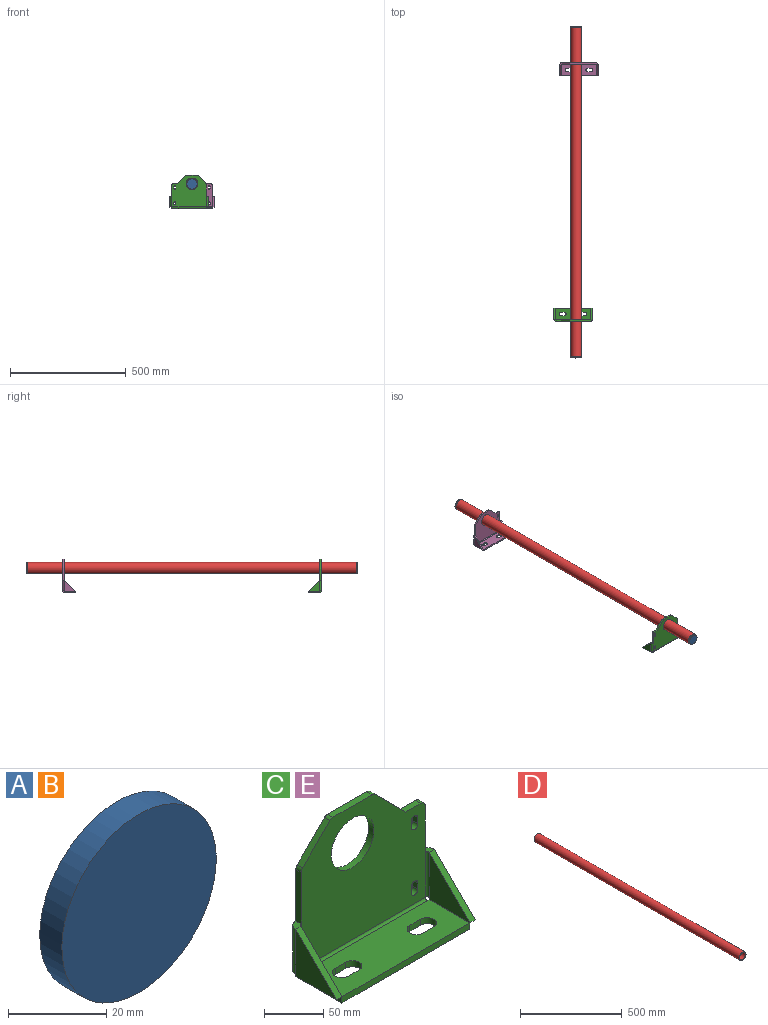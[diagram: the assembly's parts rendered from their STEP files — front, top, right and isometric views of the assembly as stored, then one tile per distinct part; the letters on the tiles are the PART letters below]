
ASSEMBLY  parts=5 mates=8
PART A: 3 faces, bbox 44.5x6.4x44.5 mm
  f0: cylinder r=22.23mm len=44.45mm, axis (0,1,0), area 886.7mm2, adj f1,f2
  f1: plane 44.45x44.45mm, normal (0,-1,0), area 1551.8mm2, adj f0
  f2: plane 44.45x44.45mm, normal (0,1,0), area 1551.8mm2, adj f0
PART B: same geometry as A
PART C: 58 faces, bbox 165.1x57.2x146.1 mm
  f0: plane 6.35x2.26mm, normal (0,1,0), area 14.4mm2, adj f1,f3,f4,f51
  f1: plane 48.51x6.35mm, normal (0,0,-1), area 308.1mm2, adj f0,f2,f3,f4
  f2: plane 48.51x48.51mm, normal (0,-0.71,0.71), area 435.7mm2, adj f1,f3,f4,f50
  f3: plane 48.51x48.51mm, normal (1,0,0), area 1176.8mm2, adj f0,f1,f2,f52
  f4: plane 48.51x48.51mm, normal (-1,0,0), area 1176.8mm2, adj f0,f1,f2,f53
  f5: plane 47.98x6.35mm, normal (1,0,0), area 304.7mm2, adj f20,f21,f50,f57
  f6: plane 6.35x6.35mm, normal (-1,0,0), area 40.3mm2, adj f7,f19,f20,f21
  f7: cylinder r=3.97mm len=7.94mm, axis (0,-1,0), area 79.2mm2, adj f6,f8,f20,f21
  f8: plane 6.35x6.35mm, normal (1,0,0), area 40.3mm2, adj f7,f19,f20,f21
  f9: plane 32.84x32.84mm, normal (-0.71,0,0.71), area 294.9mm2, adj f20,f21,f54,f55
  f10: plane 46.59x6.35mm, normal (0,0,1), area 295.9mm2, adj f20,f21,f55,f56
  f11: plane 36.61x36.61mm, normal (0.71,0,0.71), area 328.8mm2, adj f12,f20,f21,f56
  f12: plane 18.03x6.35mm, normal (0,0,1), area 114.5mm2, adj f11,f20,f21,f57
  f13: plane 6.35x6.35mm, normal (-1,0,0), area 40.3mm2, adj f14,f16,f20,f21
  f14: cylinder r=3.97mm len=7.94mm, axis (0,-1,0), area 79.2mm2, adj f13,f15,f20,f21
  f15: plane 6.35x6.35mm, normal (1,0,0), area 40.3mm2, adj f14,f16,f20,f21
  f16: cylinder r=3.97mm len=7.94mm, axis (0,-1,0), area 79.2mm2, adj f13,f15,f20,f21
  f17: cylinder r=25.4mm len=50.8mm, axis (0,-1,0), area 1013.4mm2, adj f20,f21
  f18: plane 53.24x6.35mm, normal (-1,0,0), area 338.1mm2, adj f20,f21,f28,f54
  f19: cylinder r=3.97mm len=7.94mm, axis (0,-1,0), area 79.2mm2, adj f6,f8,f20,f21
  f20: plane 147.83x137.41mm, normal (0,1,0), area 15832.1mm2, adj f5,f6,f7,f8,f9,f10,f11,f12
  f21: plane 147.83x137.41mm, normal (0,-1,0), area 15832.1mm2, adj f5,f6,f7,f8,f9,f10,f11,f12
  f22: plane 6.35x2.26mm, normal (0,1,0), area 14.4mm2, adj f23,f25,f26,f27
  f23: plane 48.51x6.35mm, normal (0,0,-1), area 308.1mm2, adj f22,f24,f25,f26
  f24: plane 48.51x48.51mm, normal (0,-0.71,0.71), area 435.7mm2, adj f23,f25,f26,f28
  f25: plane 48.51x48.51mm, normal (-1,0,0), area 1176.8mm2, adj f22,f23,f24,f29
  f26: plane 48.51x48.51mm, normal (1,0,0), area 1176.8mm2, adj f22,f23,f24,f30
  f27: plane 8.64x8.64mm, normal (0,0,-1), area 54.5mm2, adj f22,f29,f30,f47
  f28: plane 8.64x8.64mm, normal (0,0,1), area 54.5mm2, adj f18,f24,f29,f30
  f29: cylinder r=8.64mm len=46.25mm, axis (0,0,-1), area 627.4mm2, adj f20,f25,f27,f28
  f30: cylinder r=2.29mm len=46.25mm, axis (0,0,-1), area 166.1mm2, adj f21,f26,f27,f28
  f31: plane 6.35x2.26mm, normal (0,1,0), area 14.4mm2, adj f36,f44,f45,f47
  f32: plane 12.7x6.35mm, normal (0,1,0), area 80.6mm2, adj f33,f43,f44,f45
  f33: cylinder r=7.94mm len=15.88mm, axis (0,0,1), area 158.3mm2, adj f32,f34,f44,f45
  f34: plane 12.7x6.35mm, normal (0,-1,0), area 80.6mm2, adj f33,f43,f44,f45
  f35: plane 152.35x6.35mm, normal (0,-1,0), area 967.4mm2, adj f36,f42,f44,f45
  f36: plane 48.51x6.35mm, normal (-1,0,0), area 308.1mm2, adj f31,f35,f44,f45
  f37: plane 6.35x2.26mm, normal (0,1,0), area 14.4mm2, adj f42,f44,f45,f46
  f38: plane 12.7x6.35mm, normal (0,1,0), area 80.6mm2, adj f39,f41,f44,f45
  f39: cylinder r=7.94mm len=15.88mm, axis (0,0,1), area 158.3mm2, adj f38,f40,f44,f45
  f40: plane 12.7x6.35mm, normal (0,-1,0), area 80.6mm2, adj f39,f41,f44,f45
  f41: cylinder r=7.94mm len=15.88mm, axis (0,0,1), area 158.3mm2, adj f38,f40,f44,f45
  f42: plane 48.51x6.35mm, normal (1,0,0), area 308.1mm2, adj f35,f37,f44,f45
  f43: cylinder r=7.94mm len=15.88mm, axis (0,0,1), area 158.3mm2, adj f32,f34,f44,f45
  f44: plane 152.35x48.51mm, normal (0,0,-1), area 6592mm2, adj f31,f32,f33,f34,f35,f36,f37,f38
  f45: plane 152.35x48.51mm, normal (0,0,1), area 6592mm2, adj f31,f32,f33,f34,f35,f36,f37,f38
  f46: plane 8.64x8.64mm, normal (1,0,0), area 54.5mm2, adj f37,f48,f49,f51
  f47: plane 8.64x8.64mm, normal (-1,0,0), area 54.5mm2, adj f27,f31,f48,f49
  f48: cylinder r=8.64mm len=147.83mm, axis (1,0,0), area 2005.3mm2, adj f20,f44,f46,f47
  f49: cylinder r=2.29mm len=147.83mm, axis (1,0,0), area 530.8mm2, adj f21,f45,f46,f47
  f50: plane 8.64x8.64mm, normal (0,0,1), area 54.5mm2, adj f2,f5,f52,f53
  f51: plane 8.64x8.64mm, normal (0,0,-1), area 54.5mm2, adj f0,f46,f52,f53
  f52: cylinder r=8.64mm len=46.25mm, axis (0,0,1), area 627.4mm2, adj f3,f20,f50,f51
  f53: cylinder r=2.29mm len=46.25mm, axis (0,0,1), area 166.1mm2, adj f4,f21,f50,f51
  f54: cylinder r=5.08mm len=6.35mm, axis (0,1,0), area 25.3mm2, adj f9,f18,f20,f21
  f55: cylinder r=5.08mm len=6.35mm, axis (0,1,0), area 25.3mm2, adj f9,f10,f20,f21
  f56: cylinder r=5.08mm len=6.35mm, axis (0,1,0), area 25.3mm2, adj f10,f11,f20,f21
  f57: cylinder r=5.08mm len=6.35mm, axis (0,1,0), area 50.7mm2, adj f5,f12,f20,f21
PART D: 4 faces, bbox 47.6x1422.4x47.6 mm
  f0: cylinder r=20.13mm len=1422.4mm, axis (0,1,0), area 179901.4mm2, adj f2,f3
  f1: cylinder r=23.81mm len=1422.4mm, axis (0,1,0), area 212817.1mm2, adj f2,f3
  f2: plane 47.63x47.63mm, normal (0,-1,0), area 508.4mm2, adj f0,f1
  f3: plane 47.63x47.63mm, normal (0,1,0), area 508.4mm2, adj f0,f1
PART E: same geometry as C
PLACE A t=(-471.83,-189.13,-148.38)mm
PLACE B t=(-471.83,1239.62,-148.38)mm
PLACE C rot(axis=(0,0,-1),180deg) t=(-518.86,-30.38,-205.57)mm
PLACE D t=(-471.83,1233.27,-148.38)mm
PLACE E t=(-424.79,1074.52,-205.57)mm
MATE cylindrical D.f1 <-> E.f17  axis (0,1,0) through (-471.83,522.07,-148.38)mm
MATE planar D.f1 <-> B.f0  axis (0,1,0) through (-471.83,1233.27,-148.38)mm
MATE planar E.f20 <-> D.f1  axis (0,1,0) through (-461,1080.87,-190.31)mm
MATE planar D.f1 <-> A.f0  axis (0,-1,0) through (-471.83,-189.13,-148.38)mm
MATE cylindrical B.f0 <-> D.f1  axis (0,-1,0) through (-471.83,1233.27,-148.38)mm
MATE cylindrical A.f0 <-> D.f1  axis (0,1,0) through (-471.83,-189.13,-148.38)mm
MATE cylindrical D.f1 <-> C.f17  axis (0,1,0) through (-471.83,522.07,-148.38)mm
MATE planar C.f20 <-> D.f1  axis (0,-1,0) through (-410.61,-36.73,-224.56)mm
